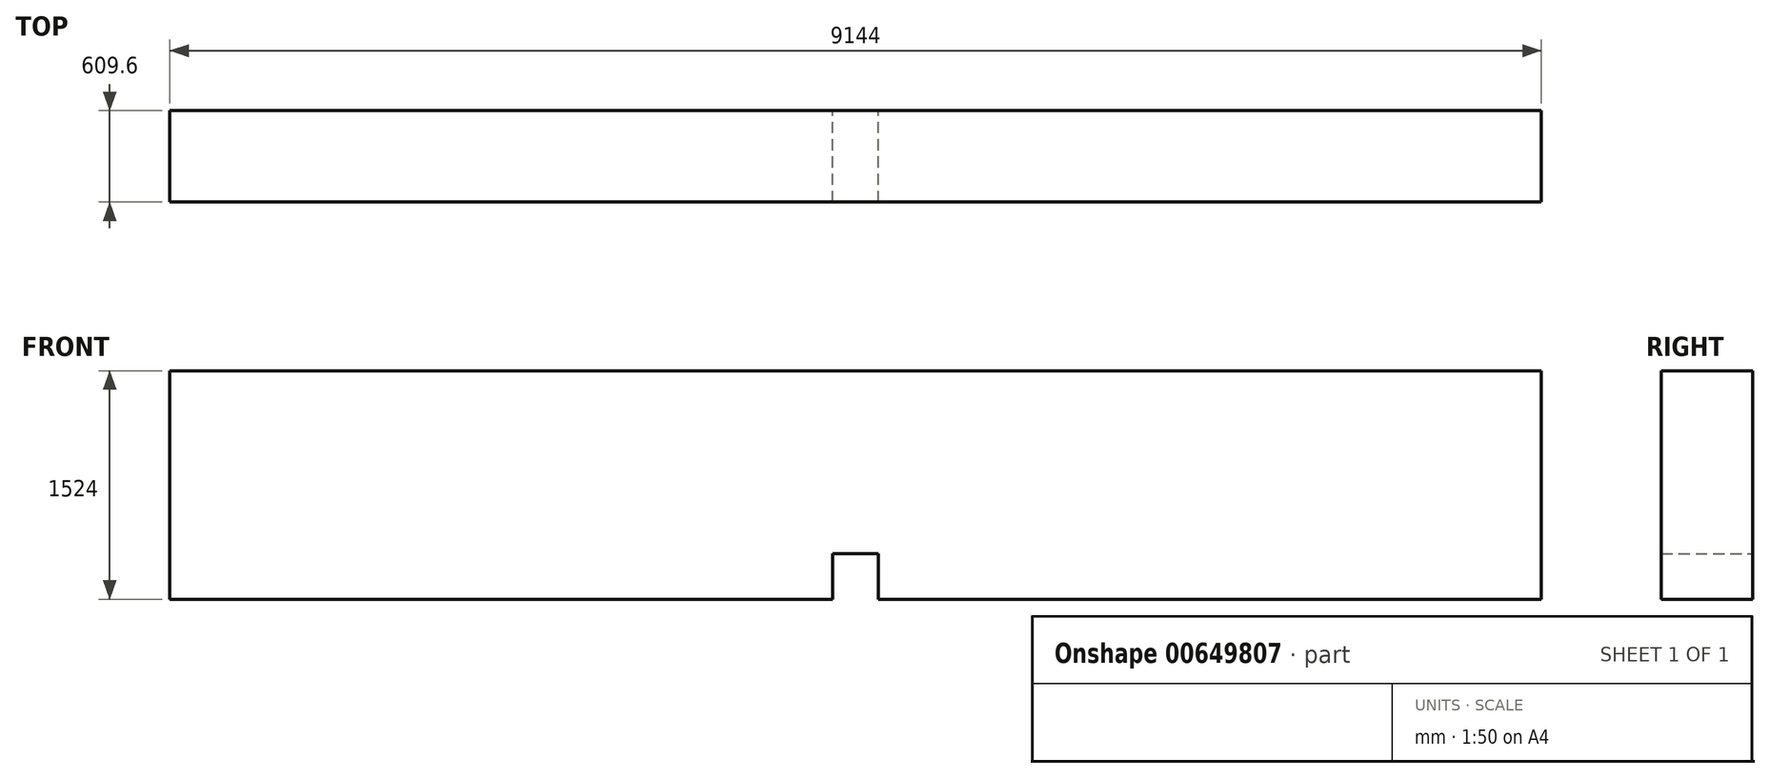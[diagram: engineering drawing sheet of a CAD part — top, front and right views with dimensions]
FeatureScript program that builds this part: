
annotation { "Feature Type Name" : "Feature", "Feature Type Description" : "" }
export const myFeature = defineFeature(function(context is Context, id is Id, definition is map)
    precondition{}
    {
        {
            var Q0;
            Q0=qCreatedBy(makeId("Front.planeOp"),FACE);
            var sketch = newSketch(context, id + "F0", { "sketchPlane" : qUnion([Q0])});
            skLineSegment(sketch, "E0", {"start": v(-4597.32, -9.89) * mm, "end": v(-177.72, -9.89) * mm});
            skLineSegment(sketch, "E1", {"start": v(-4597.32, -9.89) * mm, "end": v(-4597.32, 904.51) * mm});
            skLineSegment(sketch, "E2", {"start": v(-4597.32, 904.51) * mm, "end": v(-4597.32, 1514.11) * mm});
            skLineSegment(sketch, "E3", {"start": v(-25.32, 294.91) * mm, "end": v(127.08, 294.91) * mm});
            skLineSegment(sketch, "E4", {"start": v(-25.32, 294.91) * mm, "end": v(-177.72, 294.91) * mm});
            skLineSegment(sketch, "E5", {"start": v(-177.72, 294.91) * mm, "end": v(-177.72, -9.89) * mm});
            skLineSegment(sketch, "E6", {"start": v(127.08, 294.91) * mm, "end": v(127.08, -9.89) * mm});
            skLineSegment(sketch, "E7.trimOffspring", {"start": v(127.08, -9.89) * mm, "end": v(4546.68, -9.89) * mm});
            skLineSegment(sketch, "E8", {"start": v(4546.68, -9.89) * mm, "end": v(4546.68, 1514.11) * mm});
            skLineSegment(sketch, "E9", {"start": v(4546.68, 1514.11) * mm, "end": v(-4597.32, 1514.11) * mm});
            skSolve(sketch);
        }
        {
            var Q0;
            Q0=makeQuery(id+"F0.imprint","IMPRINT",FACE,{"disambiguationData":[TD([[makeQuery(id+"F0.imprint","IMPRINT",EDGE,{"derivedFrom":sQuery(id+"F0.wireOp",EDGE,"E0")}),1.0]])]});
            extrude(context, id + "F1", {"entities" : qUnion([Q0]), "depth" : 609.6 * mm, "offsetDistance" : 30.48 * mm});
        }
        {
            var Q0;
            Q0=sQuery(id+"F0.wireOp",EDGE,"E1");
            extrude(context, id + "F2", {"bodyType" : ToolBodyType.SURFACE, "surfaceEntities" : qUnion([Q0]), "depth" : 609.6 * mm, "offsetDistance" : 30.48 * mm});
        }
        {
            var Q0;
            Q0=sQuery(id+"F0.wireOp",EDGE,"E2");
            extrude(context, id + "F3", {"bodyType" : ToolBodyType.SURFACE, "surfaceEntities" : qUnion([Q0]), "depth" : 609.6 * mm, "offsetDistance" : 30.48 * mm});
        }
    });
